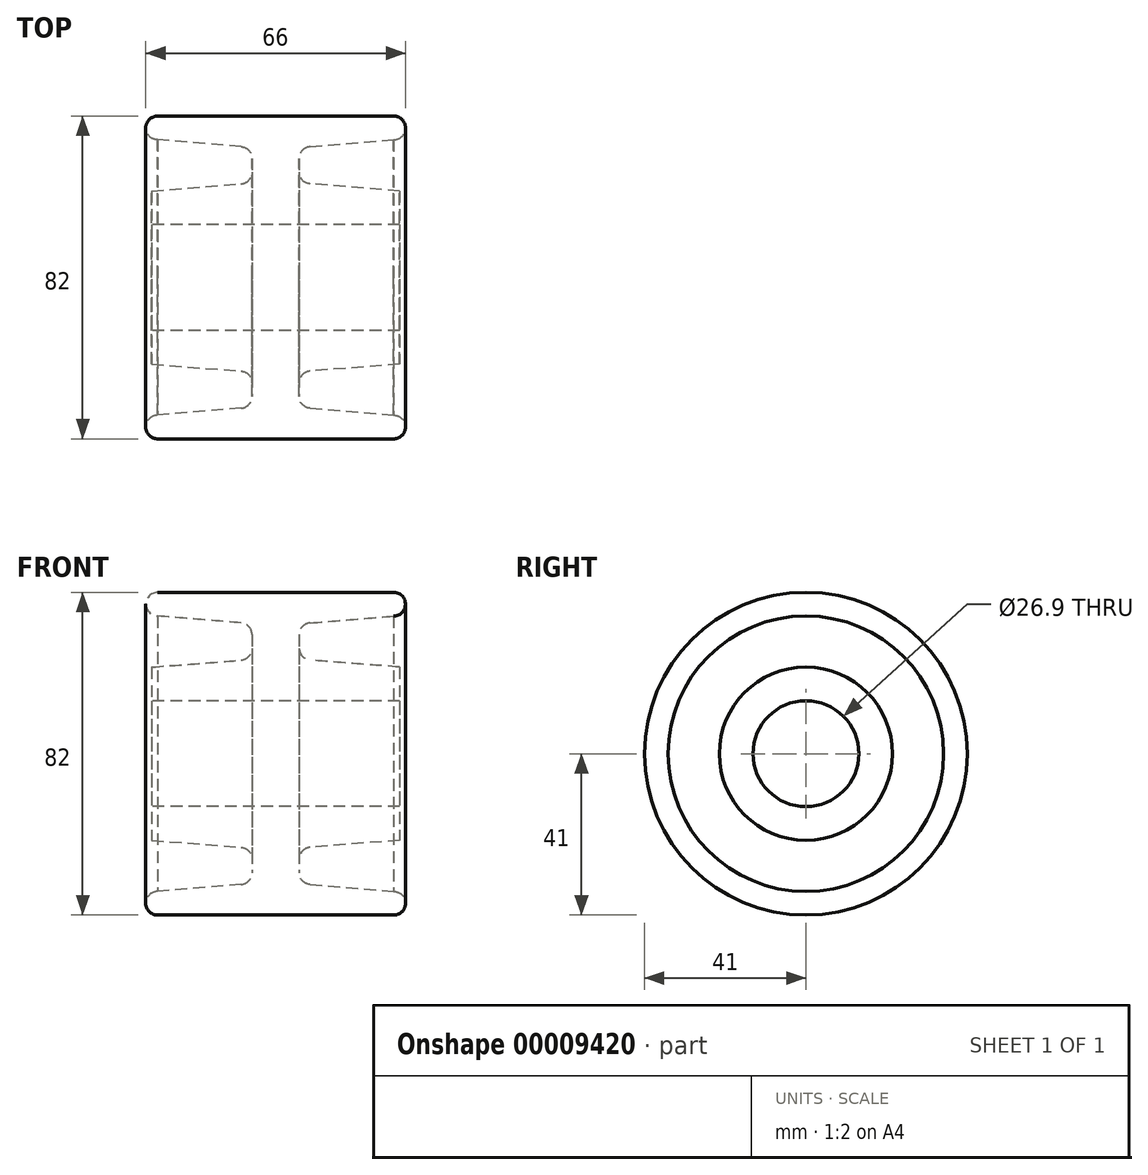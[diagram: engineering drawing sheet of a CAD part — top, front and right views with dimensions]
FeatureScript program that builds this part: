
annotation { "Feature Type Name" : "Feature", "Feature Type Description" : "" }
export const myFeature = defineFeature(function(context is Context, id is Id, definition is map)
    precondition{}
    {
        {
            var Q0;
            Q0=qCreatedBy(makeId("Front.planeOp"),FACE);
            var sketch = newSketch(context, id + "F0", { "sketchPlane" : qUnion([Q0])});
            skLineSegment(sketch, "E0", {"start": v(0, 41) * mm, "end": v(-30, 41) * mm});
            skArc(sketch, "E1", {"start": v(-30, 41) * mm, "mid": v(-33, 38) * mm, "end": v(-30, 35) * mm});
            skLineSegment(sketch, "E2", {"start": v(-8.77, 23.78) * mm, "end": v(-31.5, 22) * mm});
            skLineSegment(sketch, "E3", {"start": v(-31.5, 22) * mm, "end": v(-31.5, 13.45) * mm});
            skLineSegment(sketch, "E4", {"start": v(-31.5, 13.45) * mm, "end": v(0, 13.45) * mm});
            skLineSegment(sketch, "E5", {"start": v(-31.5, 0) * mm, "end": v(-31.5, 35.83) * mm, "construction": true});
            skLineSegment(sketch, "E6", {"start": v(-33, 0) * mm, "end": v(-33, 38) * mm, "construction": true});
            skLineSegment(sketch, "E7", {"start": v(-6, 26.77) * mm, "end": v(-6, 30.24) * mm});
            skLineSegment(sketch, "E8", {"start": v(-8.75, 33.23) * mm, "end": v(-30, 35) * mm});
            skLineSegment(sketch, "E9.0.MirrorCS", {"start": v(31.5, 13.45) * mm, "end": v(0, 13.45) * mm});
            skLineSegment(sketch, "E9.1.MirrorCS", {"start": v(8.77, 23.78) * mm, "end": v(31.5, 22) * mm});
            skLineSegment(sketch, "E9.2.MirrorCS", {"start": v(8.75, 33.23) * mm, "end": v(30, 35) * mm});
            skLineSegment(sketch, "E9.3.MirrorCS", {"start": v(6, 26.77) * mm, "end": v(6, 30.24) * mm});
            skArc(sketch, "E9.4.MirrorCS", {"start": v(30, 41) * mm, "mid": v(33, 38) * mm, "end": v(30, 35) * mm});
            skLineSegment(sketch, "E9.5.MirrorCS", {"start": v(0, 41) * mm, "end": v(30, 41) * mm});
            skLineSegment(sketch, "E9.6.MirrorCS", {"start": v(31.5, 22) * mm, "end": v(31.5, 13.45) * mm});
            skPoint(sketch, "E10.visualSharp", {"position": v(-6, 33) * mm});
            skArc(sketch, "E10.filletArc", {"start": v(-6, 30.24) * mm, "mid": v(-6.8, 32.27) * mm, "end": v(-8.75, 33.23) * mm});
            skPoint(sketch, "E11.visualSharp", {"position": v(-6, 24) * mm});
            skArc(sketch, "E11.filletArc", {"start": v(-8.77, 23.78) * mm, "mid": v(-6.8, 24.74) * mm, "end": v(-6, 26.77) * mm});
            skPoint(sketch, "E12.visualSharp", {"position": v(6, 24) * mm});
            skArc(sketch, "E12.filletArc", {"start": v(6, 26.77) * mm, "mid": v(6.8, 24.74) * mm, "end": v(8.77, 23.78) * mm});
            skPoint(sketch, "E13.visualSharp", {"position": v(6, 33) * mm});
            skArc(sketch, "E13.filletArc", {"start": v(8.75, 33.23) * mm, "mid": v(6.8, 32.27) * mm, "end": v(6, 30.24) * mm});
            skLineSegment(sketch, "E14", {"start": v(-75.79, 0) * mm, "end": v(74.9, 0) * mm, "construction": true});
            skSolve(sketch);
        }
        {
            var Q0;
            Q0=makeQuery(id+"F0.imprint","IMPRINT",FACE,{"disambiguationData":[TD([[makeQuery(id+"F0.imprint","IMPRINT",EDGE,{"derivedFrom":sQuery(id+"F0.wireOp",EDGE,"E0")}),1.0]])]});
            var Q1;
            Q1=sQuery(id+"F0.wireOp",EDGE,"E14");
            revolve(context, id + "F1", {"entities" : qUnion([Q0]), "axis" : qUnion([Q1]), "revolveType" : RevolveType.FULL});
        }
    });
